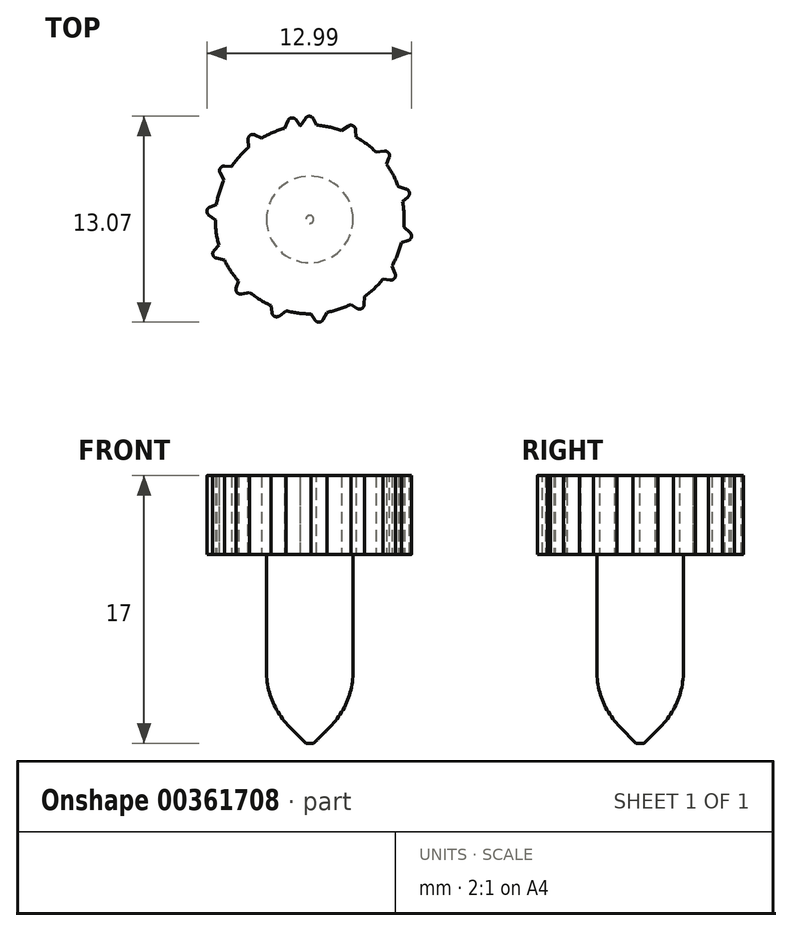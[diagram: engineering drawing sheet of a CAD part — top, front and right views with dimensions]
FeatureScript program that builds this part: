
annotation { "Feature Type Name" : "Feature", "Feature Type Description" : "" }
export const myFeature = defineFeature(function(context is Context, id is Id, definition is map)
    precondition{}
    {
        {
            var Q0;
            Q0=qCreatedBy(makeId("Top.planeOp"),FACE);
            var sketch = newSketch(context, id + "F0", { "sketchPlane" : qUnion([Q0])});
            skCircle(sketch, "E0", {"center": v(0, 0) * mm, "radius": 2.75 * mm});
            skSolve(sketch);
        }
        {
            var Q0;
            Q0 = qSketchRegion(id + "F0", true);
            extrude(context, id + "F1", {"entities" : qUnion([Q0]), "depth" : 12 * mm});
        }
        {
            var Q0;
            Q0=makeQuery(id+"F1.opExtrude","CAP_FACE",FACE,{"disambiguationData":[OSD([sQuery(id+"F0.wireOp",EDGE,"E0")])],"isStart":false});
            var sketch = newSketch(context, id + "F2", { "sketchPlane" : qUnion([Q0])});
            skCircle(sketch, "E1", {"center": v(0, 0) * mm, "radius": 6 * mm});
            skSolve(sketch);
        }
        {
            var Q0;
            Q0=makeQuery(id+"F2.imprint","IMPRINT",FACE,{"disambiguationData":[TD([[makeQuery(id+"F2.imprint","IMPRINT",EDGE,{"derivedFrom":sQuery(id+"F2.wireOp",EDGE,"E1")}),1.0]])]});
            var Q1;
            Q1=makeQuery(id+"F2.imprint","IMPRINT",FACE,{"disambiguationData":[TD([[makeQuery(id+"F2.imprint","IMPRINT",EDGE,{"derivedFrom":makeQuery(id+"F1.opExtrude","CAP_EDGE",EDGE,{"disambiguationData":[OSD([sQuery(id+"F0.wireOp",EDGE,"E0")])],"isStart":false})}),1.0]])]});
            extrude(context, id + "F3", {"entities" : qUnion([Q0, Q1]), "operationType" : NewBodyOperationType.ADD, "depth" : 5 * mm});
        }
        {
            var Q0;
            Q0=makeQuery(id+"F3.opExtrude","CAP_FACE",FACE,{"disambiguationData":[OSD([sQuery(id+"F2.wireOp",EDGE,"E1")])],"isStart":false});
            var sketch = newSketch(context, id + "F4", { "sketchPlane" : qUnion([Q0])});
            skLineSegment(sketch, "E2", {"start": v(-0.66, 5.85) * mm, "end": v(0, 6.85) * mm});
            skLineSegment(sketch, "E3", {"start": v(0, 6.85) * mm, "end": v(0.54, 5.78) * mm});
            skLineSegment(sketch, "E4", {"start": v(0.54, 5.78) * mm, "end": v(-0.66, 5.85) * mm});
            skLineSegment(sketch, "E5", {"start": v(-0.53, 6.04) * mm, "end": v(0.44, 5.98) * mm});
            skLineSegment(sketch, "E6.1.0", {"start": v(1.87, 5.58) * mm, "end": v(2.9, 6.2) * mm});
            skLineSegment(sketch, "E6.1.1", {"start": v(2.9, 6.2) * mm, "end": v(2.93, 5) * mm});
            skLineSegment(sketch, "E6.1.2", {"start": v(2.93, 5) * mm, "end": v(1.87, 5.58) * mm});
            skLineSegment(sketch, "E6.1.3", {"start": v(2.07, 5.7) * mm, "end": v(2.92, 5.24) * mm});
            skLineSegment(sketch, "E6.2.0", {"start": v(4.06, 4.26) * mm, "end": v(5.25, 4.4) * mm});
            skLineSegment(sketch, "E6.2.1", {"start": v(5.25, 4.4) * mm, "end": v(4.77, 3.3) * mm});
            skLineSegment(sketch, "E6.2.2", {"start": v(4.77, 3.3) * mm, "end": v(4.06, 4.26) * mm});
            skLineSegment(sketch, "E6.2.3", {"start": v(4.29, 4.3) * mm, "end": v(4.86, 3.51) * mm});
            skPoint(sketch, "E6.center", {"position": v(0, 0) * mm});
            skLineSegment(sketch, "E6.anchor1", {"start": v(0, 0) * mm, "end": v(-0.66, 5.85) * mm, "construction": true});
            skLineSegment(sketch, "E6.anchor2", {"start": v(0, 0) * mm, "end": v(-1.66, 5.64) * mm, "construction": true});
            skLineSegment(sketch, "E7.1.3.0", {"start": v(5.48, 2.15) * mm, "end": v(6.62, 1.77) * mm});
            skLineSegment(sketch, "E7.3.3.0", {"start": v(6.62, 1.77) * mm, "end": v(5.72, 0.97) * mm});
            skLineSegment(sketch, "E7.6.3.0", {"start": v(5.72, 0.97) * mm, "end": v(5.48, 2.15) * mm});
            skLineSegment(sketch, "E7.9.3.0", {"start": v(5.7, 2.08) * mm, "end": v(5.9, 1.13) * mm});
            skLineSegment(sketch, "E7.1.4.0", {"start": v(5.87, -0.37) * mm, "end": v(6.75, -1.19) * mm});
            skLineSegment(sketch, "E7.3.4.0", {"start": v(6.75, -1.19) * mm, "end": v(5.6, -1.53) * mm});
            skLineSegment(sketch, "E7.6.4.0", {"start": v(5.6, -1.53) * mm, "end": v(5.87, -0.37) * mm});
            skLineSegment(sketch, "E7.9.4.0", {"start": v(6.04, -0.52) * mm, "end": v(5.82, -1.47) * mm});
            skLineSegment(sketch, "E7.1.5.0", {"start": v(5.17, -2.81) * mm, "end": v(5.61, -3.93) * mm});
            skLineSegment(sketch, "E7.3.5.0", {"start": v(5.61, -3.93) * mm, "end": v(4.42, -3.76) * mm});
            skLineSegment(sketch, "E7.6.5.0", {"start": v(4.42, -3.76) * mm, "end": v(5.17, -2.81) * mm});
            skLineSegment(sketch, "E7.9.5.0", {"start": v(5.25, -3.03) * mm, "end": v(4.65, -3.79) * mm});
            skLineSegment(sketch, "E7.1.6.0", {"start": v(3.5, -4.73) * mm, "end": v(3.43, -5.93) * mm});
            skLineSegment(sketch, "E7.3.6.0", {"start": v(3.43, -5.93) * mm, "end": v(2.42, -5.27) * mm});
            skLineSegment(sketch, "E7.6.6.0", {"start": v(2.42, -5.27) * mm, "end": v(3.5, -4.73) * mm});
            skLineSegment(sketch, "E7.9.6.0", {"start": v(3.48, -4.97) * mm, "end": v(2.62, -5.4) * mm});
            skLineSegment(sketch, "E7.1.7.0", {"start": v(1.17, -5.77) * mm, "end": v(0.6, -6.82) * mm});
            skLineSegment(sketch, "E7.3.7.0", {"start": v(0.6, -6.82) * mm, "end": v(-0.03, -5.8) * mm});
            skLineSegment(sketch, "E7.6.7.0", {"start": v(-0.03, -5.8) * mm, "end": v(1.17, -5.77) * mm});
            skLineSegment(sketch, "E7.9.7.0", {"start": v(1.06, -5.97) * mm, "end": v(0.09, -6) * mm});
            skLineSegment(sketch, "E7.1.8.0", {"start": v(-1.38, -5.72) * mm, "end": v(-2.34, -6.44) * mm});
            skLineSegment(sketch, "E7.3.8.0", {"start": v(-2.34, -6.44) * mm, "end": v(-2.48, -5.25) * mm});
            skLineSegment(sketch, "E7.6.8.0", {"start": v(-2.48, -5.25) * mm, "end": v(-1.38, -5.72) * mm});
            skLineSegment(sketch, "E7.9.8.0", {"start": v(-1.57, -5.86) * mm, "end": v(-2.46, -5.48) * mm});
            skLineSegment(sketch, "E7.1.9.0", {"start": v(-3.67, -4.6) * mm, "end": v(-4.84, -4.84) * mm});
            skLineSegment(sketch, "E7.3.9.0", {"start": v(-4.84, -4.84) * mm, "end": v(-4.47, -3.7) * mm});
            skLineSegment(sketch, "E7.6.9.0", {"start": v(-4.47, -3.7) * mm, "end": v(-3.67, -4.6) * mm});
            skLineSegment(sketch, "E7.9.9.0", {"start": v(-3.9, -4.65) * mm, "end": v(-4.54, -3.92) * mm});
            skLineSegment(sketch, "E7.1.10.0", {"start": v(-5.27, -2.62) * mm, "end": v(-6.44, -2.34) * mm});
            skLineSegment(sketch, "E7.3.10.0", {"start": v(-6.44, -2.34) * mm, "end": v(-5.61, -1.47) * mm});
            skLineSegment(sketch, "E7.6.10.0", {"start": v(-5.61, -1.47) * mm, "end": v(-5.27, -2.62) * mm});
            skLineSegment(sketch, "E7.9.10.0", {"start": v(-5.5, -2.57) * mm, "end": v(-5.77, -1.64) * mm});
            skLineSegment(sketch, "E7.1.11.0", {"start": v(-5.88, -0.15) * mm, "end": v(-6.82, 0.6) * mm});
            skLineSegment(sketch, "E7.3.11.0", {"start": v(-6.82, 0.6) * mm, "end": v(-5.7, 1.04) * mm});
            skLineSegment(sketch, "E7.6.11.0", {"start": v(-5.7, 1.04) * mm, "end": v(-5.88, -0.15) * mm});
            skLineSegment(sketch, "E7.9.11.0", {"start": v(-6.06, 0) * mm, "end": v(-5.92, 0.96) * mm});
            skLineSegment(sketch, "E7.1.12.0", {"start": v(-5.4, 2.35) * mm, "end": v(-5.93, 3.43) * mm});
            skLineSegment(sketch, "E7.3.12.0", {"start": v(-5.93, 3.43) * mm, "end": v(-4.73, 3.36) * mm});
            skLineSegment(sketch, "E7.6.12.0", {"start": v(-4.73, 3.36) * mm, "end": v(-5.4, 2.35) * mm});
            skLineSegment(sketch, "E7.9.12.0", {"start": v(-5.5, 2.56) * mm, "end": v(-4.97, 3.37) * mm});
            skLineSegment(sketch, "E7.1.13.0", {"start": v(-3.9, 4.41) * mm, "end": v(-3.93, 5.61) * mm});
            skLineSegment(sketch, "E7.3.13.0", {"start": v(-3.93, 5.61) * mm, "end": v(-2.87, 5.04) * mm});
            skLineSegment(sketch, "E7.6.13.0", {"start": v(-2.87, 5.04) * mm, "end": v(-3.9, 4.41) * mm});
            skLineSegment(sketch, "E7.9.13.0", {"start": v(-3.9, 4.64) * mm, "end": v(-3.08, 5.15) * mm});
            skLineSegment(sketch, "E7.1.14.0", {"start": v(-1.66, 5.64) * mm, "end": v(-1.19, 6.75) * mm});
            skLineSegment(sketch, "E7.3.14.0", {"start": v(-1.19, 6.75) * mm, "end": v(-0.47, 5.78) * mm});
            skLineSegment(sketch, "E7.6.14.0", {"start": v(-0.47, 5.78) * mm, "end": v(-1.66, 5.64) * mm});
            skLineSegment(sketch, "E7.9.14.0", {"start": v(-1.57, 5.86) * mm, "end": v(-0.61, 5.97) * mm});
            skSolve(sketch);
        }
        {
            var Q0;
            {var subQ0=sQuery(id+"F4.wireOp",EDGE,"E3");var subQ1=sQuery(id+"F4.wireOp",EDGE,"E2");var subQ2=makeQuery(id+"F4.imprint","INTERSECT",VERTEX,{"derivedFrom":[subQ1,subQ0]});Q0=makeQuery(id+"F4.imprint","IMPRINT",FACE,{"disambiguationData":[TD([[makeQuery(id+"F4.imprint","IMPRINT",EDGE,{"disambiguationData":[TD([[subQ2,1.0]])],"derivedFrom":subQ1}),-1.0]])]});}
            var Q1;
            {var subQ0=sQuery(id+"F4.wireOp",EDGE,"E4");Q1=makeQuery(id+"F4.imprint","IMPRINT",FACE,{"disambiguationData":[TD([[makeQuery(id+"F4.imprint","IMPRINT",EDGE,{"derivedFrom":subQ0}),-1.0]])]});}
            var Q2;
            {var subQ0=sQuery(id+"F4.wireOp",EDGE,"E5");var subQ1=sQuery(id+"F4.wireOp",EDGE,"E3");var subQ2=makeQuery(id+"F4.imprint","INTERSECT",VERTEX,{"derivedFrom":[subQ1,subQ0]});Q2=makeQuery(id+"F4.imprint","IMPRINT",FACE,{"disambiguationData":[TD([[makeQuery(id+"F4.imprint","IMPRINT",EDGE,{"disambiguationData":[TD([[subQ2,-1.0]])],"derivedFrom":subQ1}),-1.0]])]});}
            var Q3;
            {var subQ0=sQuery(id+"F4.wireOp",EDGE,"E5");var subQ1=sQuery(id+"F4.wireOp",EDGE,"E2");var subQ2=makeQuery(id+"F4.imprint","INTERSECT",VERTEX,{"derivedFrom":[subQ1,subQ0]});Q3=makeQuery(id+"F4.imprint","IMPRINT",FACE,{"disambiguationData":[TD([[makeQuery(id+"F4.imprint","IMPRINT",EDGE,{"disambiguationData":[TD([[subQ2,1.0]])],"derivedFrom":subQ1}),-1.0]])]});}
            var Q4;
            {var subQ0=sQuery(id+"F4.wireOp",EDGE,"f33b821f-3d74-4163-88d8-381343337da1.3.27.0");var subQ1=sQuery(id+"F4.wireOp",EDGE,"f33b821f-3d74-4163-88d8-381343337da1.1.27.0");var subQ2=makeQuery(id+"F4.imprint","INTERSECT",VERTEX,{"derivedFrom":[subQ1,subQ0]});Q4=makeQuery(id+"F4.imprint","IMPRINT",FACE,{"disambiguationData":[TD([[makeQuery(id+"F4.imprint","IMPRINT",EDGE,{"disambiguationData":[TD([[subQ2,1.0]])],"derivedFrom":subQ1}),-1.0]])]});}
            var Q5;
            {var subQ0=sQuery(id+"F4.wireOp",EDGE,"f33b821f-3d74-4163-88d8-381343337da1.3.29.0");var subQ1=sQuery(id+"F4.wireOp",EDGE,"f33b821f-3d74-4163-88d8-381343337da1.1.29.0");var subQ2=makeQuery(id+"F4.imprint","INTERSECT",VERTEX,{"derivedFrom":[subQ1,subQ0]});Q5=makeQuery(id+"F4.imprint","IMPRINT",FACE,{"disambiguationData":[TD([[makeQuery(id+"F4.imprint","IMPRINT",EDGE,{"disambiguationData":[TD([[subQ2,1.0]])],"derivedFrom":subQ1}),-1.0]])]});}
            var Q6;
            {var subQ0=sQuery(id+"F4.wireOp",EDGE,"f33b821f-3d74-4163-88d8-381343337da1.3.26.0");var subQ1=sQuery(id+"F4.wireOp",EDGE,"f33b821f-3d74-4163-88d8-381343337da1.1.26.0");var subQ2=makeQuery(id+"F4.imprint","INTERSECT",VERTEX,{"derivedFrom":[subQ1,subQ0]});Q6=makeQuery(id+"F4.imprint","IMPRINT",FACE,{"disambiguationData":[TD([[makeQuery(id+"F4.imprint","IMPRINT",EDGE,{"disambiguationData":[TD([[subQ2,1.0]])],"derivedFrom":subQ1}),-1.0]])]});}
            var Q7;
            {var subQ0=sQuery(id+"F4.wireOp",EDGE,"E7.3.16.0");var subQ1=sQuery(id+"F4.wireOp",EDGE,"E7.1.16.0");var subQ2=makeQuery(id+"F4.imprint","INTERSECT",VERTEX,{"derivedFrom":[subQ1,subQ0]});Q7=makeQuery(id+"F4.imprint","IMPRINT",FACE,{"disambiguationData":[TD([[makeQuery(id+"F4.imprint","IMPRINT",EDGE,{"disambiguationData":[TD([[subQ2,1.0]])],"derivedFrom":subQ1}),-1.0]])]});}
            var Q8;
            {var subQ0=sQuery(id+"F4.wireOp",EDGE,"f33b821f-3d74-4163-88d8-381343337da1.3.21.0");var subQ1=sQuery(id+"F4.wireOp",EDGE,"f33b821f-3d74-4163-88d8-381343337da1.1.21.0");var subQ2=makeQuery(id+"F4.imprint","INTERSECT",VERTEX,{"derivedFrom":[subQ1,subQ0]});Q8=makeQuery(id+"F4.imprint","IMPRINT",FACE,{"disambiguationData":[TD([[makeQuery(id+"F4.imprint","IMPRINT",EDGE,{"disambiguationData":[TD([[subQ2,1.0]])],"derivedFrom":subQ1}),-1.0]])]});}
            var Q9;
            {var subQ0=sQuery(id+"F4.wireOp",EDGE,"f33b821f-3d74-4163-88d8-381343337da1.3.28.0");var subQ1=sQuery(id+"F4.wireOp",EDGE,"f33b821f-3d74-4163-88d8-381343337da1.1.28.0");var subQ2=makeQuery(id+"F4.imprint","INTERSECT",VERTEX,{"derivedFrom":[subQ1,subQ0]});Q9=makeQuery(id+"F4.imprint","IMPRINT",FACE,{"disambiguationData":[TD([[makeQuery(id+"F4.imprint","IMPRINT",EDGE,{"disambiguationData":[TD([[subQ2,1.0]])],"derivedFrom":subQ1}),-1.0]])]});}
            var Q10;
            {var subQ0=sQuery(id+"F4.wireOp",EDGE,"f33b821f-3d74-4163-88d8-381343337da1.3.25.0");var subQ1=sQuery(id+"F4.wireOp",EDGE,"f33b821f-3d74-4163-88d8-381343337da1.1.25.0");var subQ2=makeQuery(id+"F4.imprint","INTERSECT",VERTEX,{"derivedFrom":[subQ1,subQ0]});Q10=makeQuery(id+"F4.imprint","IMPRINT",FACE,{"disambiguationData":[TD([[makeQuery(id+"F4.imprint","IMPRINT",EDGE,{"disambiguationData":[TD([[subQ2,1.0]])],"derivedFrom":subQ1}),-1.0]])]});}
            var Q11;
            {var subQ0=sQuery(id+"F4.wireOp",EDGE,"f33b821f-3d74-4163-88d8-381343337da1.3.22.0");var subQ1=sQuery(id+"F4.wireOp",EDGE,"f33b821f-3d74-4163-88d8-381343337da1.1.22.0");var subQ2=makeQuery(id+"F4.imprint","INTERSECT",VERTEX,{"derivedFrom":[subQ1,subQ0]});Q11=makeQuery(id+"F4.imprint","IMPRINT",FACE,{"disambiguationData":[TD([[makeQuery(id+"F4.imprint","IMPRINT",EDGE,{"disambiguationData":[TD([[subQ2,1.0]])],"derivedFrom":subQ1}),-1.0]])]});}
            var Q12;
            {var subQ0=sQuery(id+"F4.wireOp",EDGE,"f33b821f-3d74-4163-88d8-381343337da1.3.23.0");var subQ1=sQuery(id+"F4.wireOp",EDGE,"f33b821f-3d74-4163-88d8-381343337da1.1.23.0");var subQ2=makeQuery(id+"F4.imprint","INTERSECT",VERTEX,{"derivedFrom":[subQ1,subQ0]});Q12=makeQuery(id+"F4.imprint","IMPRINT",FACE,{"disambiguationData":[TD([[makeQuery(id+"F4.imprint","IMPRINT",EDGE,{"disambiguationData":[TD([[subQ2,1.0]])],"derivedFrom":subQ1}),-1.0]])]});}
            var Q13;
            {var subQ0=sQuery(id+"F4.wireOp",EDGE,"f33b821f-3d74-4163-88d8-381343337da1.3.24.0");var subQ1=sQuery(id+"F4.wireOp",EDGE,"f33b821f-3d74-4163-88d8-381343337da1.1.24.0");var subQ2=makeQuery(id+"F4.imprint","INTERSECT",VERTEX,{"derivedFrom":[subQ1,subQ0]});Q13=makeQuery(id+"F4.imprint","IMPRINT",FACE,{"disambiguationData":[TD([[makeQuery(id+"F4.imprint","IMPRINT",EDGE,{"disambiguationData":[TD([[subQ2,1.0]])],"derivedFrom":subQ1}),-1.0]])]});}
            var Q14;
            {var subQ0=sQuery(id+"F4.wireOp",EDGE,"f33b821f-3d74-4163-88d8-381343337da1.3.20.0");var subQ1=sQuery(id+"F4.wireOp",EDGE,"f33b821f-3d74-4163-88d8-381343337da1.1.20.0");var subQ2=makeQuery(id+"F4.imprint","INTERSECT",VERTEX,{"derivedFrom":[subQ1,subQ0]});Q14=makeQuery(id+"F4.imprint","IMPRINT",FACE,{"disambiguationData":[TD([[makeQuery(id+"F4.imprint","IMPRINT",EDGE,{"disambiguationData":[TD([[subQ2,1.0]])],"derivedFrom":subQ1}),-1.0]])]});}
            var Q15;
            {var subQ0=sQuery(id+"F4.wireOp",EDGE,"E7.3.15.0");var subQ1=sQuery(id+"F4.wireOp",EDGE,"E7.1.15.0");var subQ2=makeQuery(id+"F4.imprint","INTERSECT",VERTEX,{"derivedFrom":[subQ1,subQ0]});Q15=makeQuery(id+"F4.imprint","IMPRINT",FACE,{"disambiguationData":[TD([[makeQuery(id+"F4.imprint","IMPRINT",EDGE,{"disambiguationData":[TD([[subQ2,1.0]])],"derivedFrom":subQ1}),-1.0]])]});}
            var Q16;
            {var subQ0=sQuery(id+"F4.wireOp",EDGE,"E7.3.19.0");var subQ1=sQuery(id+"F4.wireOp",EDGE,"E7.1.19.0");var subQ2=makeQuery(id+"F4.imprint","INTERSECT",VERTEX,{"derivedFrom":[subQ1,subQ0]});Q16=makeQuery(id+"F4.imprint","IMPRINT",FACE,{"disambiguationData":[TD([[makeQuery(id+"F4.imprint","IMPRINT",EDGE,{"disambiguationData":[TD([[subQ2,1.0]])],"derivedFrom":subQ1}),-1.0]])]});}
            var Q17;
            {var subQ0=sQuery(id+"F4.wireOp",EDGE,"E7.3.18.0");var subQ1=sQuery(id+"F4.wireOp",EDGE,"E7.1.18.0");var subQ2=makeQuery(id+"F4.imprint","INTERSECT",VERTEX,{"derivedFrom":[subQ1,subQ0]});Q17=makeQuery(id+"F4.imprint","IMPRINT",FACE,{"disambiguationData":[TD([[makeQuery(id+"F4.imprint","IMPRINT",EDGE,{"disambiguationData":[TD([[subQ2,1.0]])],"derivedFrom":subQ1}),-1.0]])]});}
            var Q18;
            {var subQ0=sQuery(id+"F4.wireOp",EDGE,"E7.3.17.0");var subQ1=sQuery(id+"F4.wireOp",EDGE,"E7.1.17.0");var subQ2=makeQuery(id+"F4.imprint","INTERSECT",VERTEX,{"derivedFrom":[subQ1,subQ0]});Q18=makeQuery(id+"F4.imprint","IMPRINT",FACE,{"disambiguationData":[TD([[makeQuery(id+"F4.imprint","IMPRINT",EDGE,{"disambiguationData":[TD([[subQ2,1.0]])],"derivedFrom":subQ1}),-1.0]])]});}
            var Q19;
            {var subQ0=sQuery(id+"F4.wireOp",EDGE,"E7.3.12.0");var subQ1=sQuery(id+"F4.wireOp",EDGE,"E7.1.12.0");var subQ2=makeQuery(id+"F4.imprint","INTERSECT",VERTEX,{"derivedFrom":[subQ1,subQ0]});Q19=makeQuery(id+"F4.imprint","IMPRINT",FACE,{"disambiguationData":[TD([[makeQuery(id+"F4.imprint","IMPRINT",EDGE,{"disambiguationData":[TD([[subQ2,1.0]])],"derivedFrom":subQ1}),-1.0]])]});}
            var Q20;
            {var subQ0=sQuery(id+"F4.wireOp",EDGE,"E7.3.11.0");var subQ1=sQuery(id+"F4.wireOp",EDGE,"E7.1.11.0");var subQ2=makeQuery(id+"F4.imprint","INTERSECT",VERTEX,{"derivedFrom":[subQ1,subQ0]});Q20=makeQuery(id+"F4.imprint","IMPRINT",FACE,{"disambiguationData":[TD([[makeQuery(id+"F4.imprint","IMPRINT",EDGE,{"disambiguationData":[TD([[subQ2,1.0]])],"derivedFrom":subQ1}),-1.0]])]});}
            var Q21;
            {var subQ0=sQuery(id+"F4.wireOp",EDGE,"E7.3.10.0");var subQ1=sQuery(id+"F4.wireOp",EDGE,"E7.1.10.0");var subQ2=makeQuery(id+"F4.imprint","INTERSECT",VERTEX,{"derivedFrom":[subQ1,subQ0]});Q21=makeQuery(id+"F4.imprint","IMPRINT",FACE,{"disambiguationData":[TD([[makeQuery(id+"F4.imprint","IMPRINT",EDGE,{"disambiguationData":[TD([[subQ2,1.0]])],"derivedFrom":subQ1}),-1.0]])]});}
            var Q22;
            {var subQ0=sQuery(id+"F4.wireOp",EDGE,"E7.3.8.0");var subQ1=sQuery(id+"F4.wireOp",EDGE,"E7.1.8.0");var subQ2=makeQuery(id+"F4.imprint","INTERSECT",VERTEX,{"derivedFrom":[subQ1,subQ0]});Q22=makeQuery(id+"F4.imprint","IMPRINT",FACE,{"disambiguationData":[TD([[makeQuery(id+"F4.imprint","IMPRINT",EDGE,{"disambiguationData":[TD([[subQ2,1.0]])],"derivedFrom":subQ1}),-1.0]])]});}
            var Q23;
            {var subQ0=sQuery(id+"F4.wireOp",EDGE,"E7.3.7.0");var subQ1=sQuery(id+"F4.wireOp",EDGE,"E7.1.7.0");var subQ2=makeQuery(id+"F4.imprint","INTERSECT",VERTEX,{"derivedFrom":[subQ1,subQ0]});Q23=makeQuery(id+"F4.imprint","IMPRINT",FACE,{"disambiguationData":[TD([[makeQuery(id+"F4.imprint","IMPRINT",EDGE,{"disambiguationData":[TD([[subQ2,1.0]])],"derivedFrom":subQ1}),-1.0]])]});}
            var Q24;
            {var subQ0=sQuery(id+"F4.wireOp",EDGE,"E7.3.6.0");var subQ1=sQuery(id+"F4.wireOp",EDGE,"E7.1.6.0");var subQ2=makeQuery(id+"F4.imprint","INTERSECT",VERTEX,{"derivedFrom":[subQ1,subQ0]});Q24=makeQuery(id+"F4.imprint","IMPRINT",FACE,{"disambiguationData":[TD([[makeQuery(id+"F4.imprint","IMPRINT",EDGE,{"disambiguationData":[TD([[subQ2,1.0]])],"derivedFrom":subQ1}),-1.0]])]});}
            var Q25;
            {var subQ0=sQuery(id+"F4.wireOp",EDGE,"E7.3.5.0");var subQ1=sQuery(id+"F4.wireOp",EDGE,"E7.1.5.0");var subQ2=makeQuery(id+"F4.imprint","INTERSECT",VERTEX,{"derivedFrom":[subQ1,subQ0]});Q25=makeQuery(id+"F4.imprint","IMPRINT",FACE,{"disambiguationData":[TD([[makeQuery(id+"F4.imprint","IMPRINT",EDGE,{"disambiguationData":[TD([[subQ2,1.0]])],"derivedFrom":subQ1}),-1.0]])]});}
            var Q26;
            {var subQ0=sQuery(id+"F4.wireOp",EDGE,"E7.3.4.0");var subQ1=sQuery(id+"F4.wireOp",EDGE,"E7.1.4.0");var subQ2=makeQuery(id+"F4.imprint","INTERSECT",VERTEX,{"derivedFrom":[subQ1,subQ0]});Q26=makeQuery(id+"F4.imprint","IMPRINT",FACE,{"disambiguationData":[TD([[makeQuery(id+"F4.imprint","IMPRINT",EDGE,{"disambiguationData":[TD([[subQ2,1.0]])],"derivedFrom":subQ1}),-1.0]])]});}
            var Q27;
            {var subQ0=sQuery(id+"F4.wireOp",EDGE,"E7.3.3.0");var subQ1=sQuery(id+"F4.wireOp",EDGE,"E7.1.3.0");var subQ2=makeQuery(id+"F4.imprint","INTERSECT",VERTEX,{"derivedFrom":[subQ1,subQ0]});Q27=makeQuery(id+"F4.imprint","IMPRINT",FACE,{"disambiguationData":[TD([[makeQuery(id+"F4.imprint","IMPRINT",EDGE,{"disambiguationData":[TD([[subQ2,1.0]])],"derivedFrom":subQ1}),-1.0]])]});}
            var Q28;
            {var subQ0=sQuery(id+"F4.wireOp",EDGE,"E6.2.1");var subQ1=sQuery(id+"F4.wireOp",EDGE,"E6.2.0");var subQ2=makeQuery(id+"F4.imprint","INTERSECT",VERTEX,{"derivedFrom":[subQ1,subQ0]});Q28=makeQuery(id+"F4.imprint","IMPRINT",FACE,{"disambiguationData":[TD([[makeQuery(id+"F4.imprint","IMPRINT",EDGE,{"disambiguationData":[TD([[subQ2,1.0]])],"derivedFrom":subQ1}),-1.0]])]});}
            var Q29;
            {var subQ0=sQuery(id+"F4.wireOp",EDGE,"E6.1.1");var subQ1=sQuery(id+"F4.wireOp",EDGE,"E6.1.0");var subQ2=makeQuery(id+"F4.imprint","INTERSECT",VERTEX,{"derivedFrom":[subQ1,subQ0]});Q29=makeQuery(id+"F4.imprint","IMPRINT",FACE,{"disambiguationData":[TD([[makeQuery(id+"F4.imprint","IMPRINT",EDGE,{"disambiguationData":[TD([[subQ2,1.0]])],"derivedFrom":subQ1}),-1.0]])]});}
            var Q30;
            {var subQ0=sQuery(id+"F4.wireOp",EDGE,"E7.3.14.0");var subQ1=sQuery(id+"F4.wireOp",EDGE,"E7.1.14.0");var subQ2=makeQuery(id+"F4.imprint","INTERSECT",VERTEX,{"derivedFrom":[subQ1,subQ0]});Q30=makeQuery(id+"F4.imprint","IMPRINT",FACE,{"disambiguationData":[TD([[makeQuery(id+"F4.imprint","IMPRINT",EDGE,{"disambiguationData":[TD([[subQ2,1.0]])],"derivedFrom":subQ1}),-1.0]])]});}
            var Q31;
            {var subQ0=sQuery(id+"F4.wireOp",EDGE,"E7.3.13.0");var subQ1=sQuery(id+"F4.wireOp",EDGE,"E7.1.13.0");var subQ2=makeQuery(id+"F4.imprint","INTERSECT",VERTEX,{"derivedFrom":[subQ1,subQ0]});Q31=makeQuery(id+"F4.imprint","IMPRINT",FACE,{"disambiguationData":[TD([[makeQuery(id+"F4.imprint","IMPRINT",EDGE,{"disambiguationData":[TD([[subQ2,1.0]])],"derivedFrom":subQ1}),-1.0]])]});}
            var Q32;
            {var subQ0=sQuery(id+"F4.wireOp",EDGE,"E7.9.6.0");var subQ1=sQuery(id+"F4.wireOp",EDGE,"E7.3.6.0");var subQ2=makeQuery(id+"F4.imprint","INTERSECT",VERTEX,{"derivedFrom":[subQ1,subQ0]});Q32=makeQuery(id+"F4.imprint","IMPRINT",FACE,{"disambiguationData":[TD([[makeQuery(id+"F4.imprint","IMPRINT",EDGE,{"disambiguationData":[TD([[subQ2,-1.0]])],"derivedFrom":subQ1}),-1.0]])]});}
            var Q33;
            {var subQ4=sQuery(id+"F4.wireOp",EDGE,"E7.6.4.0");Q33=makeQuery(id+"F4.imprint","IMPRINT",FACE,{"disambiguationData":[TD([[makeQuery(id+"F4.imprint","IMPRINT",EDGE,{"derivedFrom":subQ4}),-1.0]])]});}
            var Q34;
            {var subQ4=sQuery(id+"F4.wireOp",EDGE,"E7.6.17.0");Q34=makeQuery(id+"F4.imprint","IMPRINT",FACE,{"disambiguationData":[TD([[makeQuery(id+"F4.imprint","IMPRINT",EDGE,{"derivedFrom":subQ4}),-1.0]])]});}
            var Q35;
            {var subQ4=sQuery(id+"F4.wireOp",EDGE,"E6.1.2");Q35=makeQuery(id+"F4.imprint","IMPRINT",FACE,{"disambiguationData":[TD([[makeQuery(id+"F4.imprint","IMPRINT",EDGE,{"derivedFrom":subQ4}),-1.0]])]});}
            var Q36;
            {var subQ0=sQuery(id+"F4.wireOp",EDGE,"f33b821f-3d74-4163-88d8-381343337da1.9.22.0");var subQ1=sQuery(id+"F4.wireOp",EDGE,"f33b821f-3d74-4163-88d8-381343337da1.3.22.0");var subQ2=makeQuery(id+"F4.imprint","INTERSECT",VERTEX,{"derivedFrom":[subQ1,subQ0]});Q36=makeQuery(id+"F4.imprint","IMPRINT",FACE,{"disambiguationData":[TD([[makeQuery(id+"F4.imprint","IMPRINT",EDGE,{"disambiguationData":[TD([[subQ2,-1.0]])],"derivedFrom":subQ1}),-1.0]])]});}
            var Q37;
            {var subQ0=sQuery(id+"F4.wireOp",EDGE,"f33b821f-3d74-4163-88d8-381343337da1.6.20.0");Q37=makeQuery(id+"F4.imprint","IMPRINT",FACE,{"disambiguationData":[TD([[makeQuery(id+"F4.imprint","IMPRINT",EDGE,{"derivedFrom":subQ0}),-1.0]])]});}
            var Q38;
            {var subQ4=sQuery(id+"F4.wireOp",EDGE,"E7.6.3.0");Q38=makeQuery(id+"F4.imprint","IMPRINT",FACE,{"disambiguationData":[TD([[makeQuery(id+"F4.imprint","IMPRINT",EDGE,{"derivedFrom":subQ4}),-1.0]])]});}
            var Q39;
            {var subQ4=sQuery(id+"F4.wireOp",EDGE,"E7.6.19.0");Q39=makeQuery(id+"F4.imprint","IMPRINT",FACE,{"disambiguationData":[TD([[makeQuery(id+"F4.imprint","IMPRINT",EDGE,{"derivedFrom":subQ4}),-1.0]])]});}
            var Q40;
            {var subQ0=sQuery(id+"F4.wireOp",EDGE,"E7.6.15.0");Q40=makeQuery(id+"F4.imprint","IMPRINT",FACE,{"disambiguationData":[TD([[makeQuery(id+"F4.imprint","IMPRINT",EDGE,{"derivedFrom":subQ0}),-1.0]])]});}
            var Q41;
            {var subQ0=sQuery(id+"F4.wireOp",EDGE,"f33b821f-3d74-4163-88d8-381343337da1.9.22.0");var subQ1=sQuery(id+"F4.wireOp",EDGE,"f33b821f-3d74-4163-88d8-381343337da1.1.22.0");var subQ2=makeQuery(id+"F4.imprint","INTERSECT",VERTEX,{"derivedFrom":[subQ1,subQ0]});Q41=makeQuery(id+"F4.imprint","IMPRINT",FACE,{"disambiguationData":[TD([[makeQuery(id+"F4.imprint","IMPRINT",EDGE,{"disambiguationData":[TD([[subQ2,1.0]])],"derivedFrom":subQ1}),-1.0]])]});}
            var Q42;
            {var subQ4=sQuery(id+"F4.wireOp",EDGE,"E7.6.16.0");Q42=makeQuery(id+"F4.imprint","IMPRINT",FACE,{"disambiguationData":[TD([[makeQuery(id+"F4.imprint","IMPRINT",EDGE,{"derivedFrom":subQ4}),-1.0]])]});}
            var Q43;
            {var subQ0=sQuery(id+"F4.wireOp",EDGE,"E7.9.16.0");var subQ1=sQuery(id+"F4.wireOp",EDGE,"E7.3.16.0");var subQ2=makeQuery(id+"F4.imprint","INTERSECT",VERTEX,{"derivedFrom":[subQ1,subQ0]});Q43=makeQuery(id+"F4.imprint","IMPRINT",FACE,{"disambiguationData":[TD([[makeQuery(id+"F4.imprint","IMPRINT",EDGE,{"disambiguationData":[TD([[subQ2,-1.0]])],"derivedFrom":subQ1}),-1.0]])]});}
            var Q44;
            {var subQ4=sQuery(id+"F4.wireOp",EDGE,"f33b821f-3d74-4163-88d8-381343337da1.6.22.0");Q44=makeQuery(id+"F4.imprint","IMPRINT",FACE,{"disambiguationData":[TD([[makeQuery(id+"F4.imprint","IMPRINT",EDGE,{"derivedFrom":subQ4}),-1.0]])]});}
            var Q45;
            {var subQ0=sQuery(id+"F4.wireOp",EDGE,"E7.9.17.0");var subQ1=sQuery(id+"F4.wireOp",EDGE,"E7.1.17.0");var subQ2=makeQuery(id+"F4.imprint","INTERSECT",VERTEX,{"derivedFrom":[subQ1,subQ0]});Q45=makeQuery(id+"F4.imprint","IMPRINT",FACE,{"disambiguationData":[TD([[makeQuery(id+"F4.imprint","IMPRINT",EDGE,{"disambiguationData":[TD([[subQ2,1.0]])],"derivedFrom":subQ1}),-1.0]])]});}
            var Q46;
            {var subQ0=sQuery(id+"F4.wireOp",EDGE,"f33b821f-3d74-4163-88d8-381343337da1.9.25.0");var subQ1=sQuery(id+"F4.wireOp",EDGE,"f33b821f-3d74-4163-88d8-381343337da1.1.25.0");var subQ2=makeQuery(id+"F4.imprint","INTERSECT",VERTEX,{"derivedFrom":[subQ1,subQ0]});Q46=makeQuery(id+"F4.imprint","IMPRINT",FACE,{"disambiguationData":[TD([[makeQuery(id+"F4.imprint","IMPRINT",EDGE,{"disambiguationData":[TD([[subQ2,1.0]])],"derivedFrom":subQ1}),-1.0]])]});}
            var Q47;
            {var subQ0=sQuery(id+"F4.wireOp",EDGE,"f33b821f-3d74-4163-88d8-381343337da1.9.21.0");var subQ1=sQuery(id+"F4.wireOp",EDGE,"f33b821f-3d74-4163-88d8-381343337da1.3.21.0");var subQ2=makeQuery(id+"F4.imprint","INTERSECT",VERTEX,{"derivedFrom":[subQ1,subQ0]});Q47=makeQuery(id+"F4.imprint","IMPRINT",FACE,{"disambiguationData":[TD([[makeQuery(id+"F4.imprint","IMPRINT",EDGE,{"disambiguationData":[TD([[subQ2,-1.0]])],"derivedFrom":subQ1}),-1.0]])]});}
            var Q48;
            {var subQ4=sQuery(id+"F4.wireOp",EDGE,"f33b821f-3d74-4163-88d8-381343337da1.6.21.0");Q48=makeQuery(id+"F4.imprint","IMPRINT",FACE,{"disambiguationData":[TD([[makeQuery(id+"F4.imprint","IMPRINT",EDGE,{"derivedFrom":subQ4}),-1.0]])]});}
            var Q49;
            {var subQ4=sQuery(id+"F4.wireOp",EDGE,"E7.6.11.0");Q49=makeQuery(id+"F4.imprint","IMPRINT",FACE,{"disambiguationData":[TD([[makeQuery(id+"F4.imprint","IMPRINT",EDGE,{"derivedFrom":subQ4}),-1.0]])]});}
            var Q50;
            {var subQ4=sQuery(id+"F4.wireOp",EDGE,"E6.2.2");Q50=makeQuery(id+"F4.imprint","IMPRINT",FACE,{"disambiguationData":[TD([[makeQuery(id+"F4.imprint","IMPRINT",EDGE,{"derivedFrom":subQ4}),-1.0]])]});}
            var Q51;
            {var subQ0=sQuery(id+"F4.wireOp",EDGE,"E7.9.4.0");var subQ1=sQuery(id+"F4.wireOp",EDGE,"E7.1.4.0");var subQ2=makeQuery(id+"F4.imprint","INTERSECT",VERTEX,{"derivedFrom":[subQ1,subQ0]});Q51=makeQuery(id+"F4.imprint","IMPRINT",FACE,{"disambiguationData":[TD([[makeQuery(id+"F4.imprint","IMPRINT",EDGE,{"disambiguationData":[TD([[subQ2,1.0]])],"derivedFrom":subQ1}),-1.0]])]});}
            var Q52;
            {var subQ4=sQuery(id+"F4.wireOp",EDGE,"f33b821f-3d74-4163-88d8-381343337da1.6.28.0");Q52=makeQuery(id+"F4.imprint","IMPRINT",FACE,{"disambiguationData":[TD([[makeQuery(id+"F4.imprint","IMPRINT",EDGE,{"derivedFrom":subQ4}),-1.0]])]});}
            var Q53;
            {var subQ4=sQuery(id+"F4.wireOp",EDGE,"E7.6.12.0");Q53=makeQuery(id+"F4.imprint","IMPRINT",FACE,{"disambiguationData":[TD([[makeQuery(id+"F4.imprint","IMPRINT",EDGE,{"derivedFrom":subQ4}),-1.0]])]});}
            var Q54;
            {var subQ0=sQuery(id+"F4.wireOp",EDGE,"f33b821f-3d74-4163-88d8-381343337da1.9.28.0");var subQ1=sQuery(id+"F4.wireOp",EDGE,"f33b821f-3d74-4163-88d8-381343337da1.1.28.0");var subQ2=makeQuery(id+"F4.imprint","INTERSECT",VERTEX,{"derivedFrom":[subQ1,subQ0]});Q54=makeQuery(id+"F4.imprint","IMPRINT",FACE,{"disambiguationData":[TD([[makeQuery(id+"F4.imprint","IMPRINT",EDGE,{"disambiguationData":[TD([[subQ2,1.0]])],"derivedFrom":subQ1}),-1.0]])]});}
            var Q55;
            {var subQ0=sQuery(id+"F4.wireOp",EDGE,"f33b821f-3d74-4163-88d8-381343337da1.9.20.0");var subQ1=sQuery(id+"F4.wireOp",EDGE,"f33b821f-3d74-4163-88d8-381343337da1.1.20.0");var subQ2=makeQuery(id+"F4.imprint","INTERSECT",VERTEX,{"derivedFrom":[subQ1,subQ0]});Q55=makeQuery(id+"F4.imprint","IMPRINT",FACE,{"disambiguationData":[TD([[makeQuery(id+"F4.imprint","IMPRINT",EDGE,{"disambiguationData":[TD([[subQ2,1.0]])],"derivedFrom":subQ1}),-1.0]])]});}
            var Q56;
            {var subQ0=sQuery(id+"F4.wireOp",EDGE,"E7.9.4.0");var subQ1=sQuery(id+"F4.wireOp",EDGE,"E7.3.4.0");var subQ2=makeQuery(id+"F4.imprint","INTERSECT",VERTEX,{"derivedFrom":[subQ1,subQ0]});Q56=makeQuery(id+"F4.imprint","IMPRINT",FACE,{"disambiguationData":[TD([[makeQuery(id+"F4.imprint","IMPRINT",EDGE,{"disambiguationData":[TD([[subQ2,-1.0]])],"derivedFrom":subQ1}),-1.0]])]});}
            var Q57;
            {var subQ4=sQuery(id+"F4.wireOp",EDGE,"f33b821f-3d74-4163-88d8-381343337da1.6.29.0");Q57=makeQuery(id+"F4.imprint","IMPRINT",FACE,{"disambiguationData":[TD([[makeQuery(id+"F4.imprint","IMPRINT",EDGE,{"derivedFrom":subQ4}),-1.0]])]});}
            var Q58;
            {var subQ4=sQuery(id+"F4.wireOp",EDGE,"E7.6.13.0");Q58=makeQuery(id+"F4.imprint","IMPRINT",FACE,{"disambiguationData":[TD([[makeQuery(id+"F4.imprint","IMPRINT",EDGE,{"derivedFrom":subQ4}),-1.0]])]});}
            var Q59;
            {var subQ0=sQuery(id+"F4.wireOp",EDGE,"f33b821f-3d74-4163-88d8-381343337da1.9.20.0");var subQ1=sQuery(id+"F4.wireOp",EDGE,"f33b821f-3d74-4163-88d8-381343337da1.3.20.0");var subQ2=makeQuery(id+"F4.imprint","INTERSECT",VERTEX,{"derivedFrom":[subQ1,subQ0]});Q59=makeQuery(id+"F4.imprint","IMPRINT",FACE,{"disambiguationData":[TD([[makeQuery(id+"F4.imprint","IMPRINT",EDGE,{"disambiguationData":[TD([[subQ2,-1.0]])],"derivedFrom":subQ1}),-1.0]])]});}
            var Q60;
            {var subQ4=sQuery(id+"F4.wireOp",EDGE,"E7.6.14.0");Q60=makeQuery(id+"F4.imprint","IMPRINT",FACE,{"disambiguationData":[TD([[makeQuery(id+"F4.imprint","IMPRINT",EDGE,{"derivedFrom":subQ4}),-1.0]])]});}
            var Q61;
            {var subQ0=sQuery(id+"F4.wireOp",EDGE,"f33b821f-3d74-4163-88d8-381343337da1.9.21.0");var subQ1=sQuery(id+"F4.wireOp",EDGE,"f33b821f-3d74-4163-88d8-381343337da1.1.21.0");var subQ2=makeQuery(id+"F4.imprint","INTERSECT",VERTEX,{"derivedFrom":[subQ1,subQ0]});Q61=makeQuery(id+"F4.imprint","IMPRINT",FACE,{"disambiguationData":[TD([[makeQuery(id+"F4.imprint","IMPRINT",EDGE,{"disambiguationData":[TD([[subQ2,1.0]])],"derivedFrom":subQ1}),-1.0]])]});}
            var Q62;
            {var subQ4=sQuery(id+"F4.wireOp",EDGE,"f33b821f-3d74-4163-88d8-381343337da1.6.26.0");Q62=makeQuery(id+"F4.imprint","IMPRINT",FACE,{"disambiguationData":[TD([[makeQuery(id+"F4.imprint","IMPRINT",EDGE,{"derivedFrom":subQ4}),-1.0]])]});}
            var Q63;
            {var subQ0=sQuery(id+"F4.wireOp",EDGE,"f33b821f-3d74-4163-88d8-381343337da1.6.25.0");Q63=makeQuery(id+"F4.imprint","IMPRINT",FACE,{"disambiguationData":[TD([[makeQuery(id+"F4.imprint","IMPRINT",EDGE,{"derivedFrom":subQ0}),-1.0]])]});}
            var Q64;
            {var subQ0=sQuery(id+"F4.wireOp",EDGE,"E6.2.3");var subQ1=sQuery(id+"F4.wireOp",EDGE,"E6.2.1");var subQ2=makeQuery(id+"F4.imprint","INTERSECT",VERTEX,{"derivedFrom":[subQ1,subQ0]});Q64=makeQuery(id+"F4.imprint","IMPRINT",FACE,{"disambiguationData":[TD([[makeQuery(id+"F4.imprint","IMPRINT",EDGE,{"disambiguationData":[TD([[subQ2,-1.0]])],"derivedFrom":subQ1}),-1.0]])]});}
            var Q65;
            {var subQ4=sQuery(id+"F4.wireOp",EDGE,"E7.6.8.0");Q65=makeQuery(id+"F4.imprint","IMPRINT",FACE,{"disambiguationData":[TD([[makeQuery(id+"F4.imprint","IMPRINT",EDGE,{"derivedFrom":subQ4}),-1.0]])]});}
            var Q66;
            {var subQ4=sQuery(id+"F4.wireOp",EDGE,"f33b821f-3d74-4163-88d8-381343337da1.6.24.0");Q66=makeQuery(id+"F4.imprint","IMPRINT",FACE,{"disambiguationData":[TD([[makeQuery(id+"F4.imprint","IMPRINT",EDGE,{"derivedFrom":subQ4}),-1.0]])]});}
            var Q67;
            {var subQ0=sQuery(id+"F4.wireOp",EDGE,"E6.2.3");var subQ1=sQuery(id+"F4.wireOp",EDGE,"E6.2.0");var subQ2=makeQuery(id+"F4.imprint","INTERSECT",VERTEX,{"derivedFrom":[subQ1,subQ0]});Q67=makeQuery(id+"F4.imprint","IMPRINT",FACE,{"disambiguationData":[TD([[makeQuery(id+"F4.imprint","IMPRINT",EDGE,{"disambiguationData":[TD([[subQ2,1.0]])],"derivedFrom":subQ1}),-1.0]])]});}
            var Q68;
            {var subQ4=sQuery(id+"F4.wireOp",EDGE,"E7.6.7.0");Q68=makeQuery(id+"F4.imprint","IMPRINT",FACE,{"disambiguationData":[TD([[makeQuery(id+"F4.imprint","IMPRINT",EDGE,{"derivedFrom":subQ4}),-1.0]])]});}
            var Q69;
            {var subQ4=sQuery(id+"F4.wireOp",EDGE,"f33b821f-3d74-4163-88d8-381343337da1.6.23.0");Q69=makeQuery(id+"F4.imprint","IMPRINT",FACE,{"disambiguationData":[TD([[makeQuery(id+"F4.imprint","IMPRINT",EDGE,{"derivedFrom":subQ4}),-1.0]])]});}
            var Q70;
            {var subQ0=sQuery(id+"F4.wireOp",EDGE,"E6.1.3");var subQ1=sQuery(id+"F4.wireOp",EDGE,"E6.1.1");var subQ2=makeQuery(id+"F4.imprint","INTERSECT",VERTEX,{"derivedFrom":[subQ1,subQ0]});Q70=makeQuery(id+"F4.imprint","IMPRINT",FACE,{"disambiguationData":[TD([[makeQuery(id+"F4.imprint","IMPRINT",EDGE,{"disambiguationData":[TD([[subQ2,-1.0]])],"derivedFrom":subQ1}),-1.0]])]});}
            var Q71;
            {var subQ0=sQuery(id+"F4.wireOp",EDGE,"E7.9.17.0");var subQ1=sQuery(id+"F4.wireOp",EDGE,"E7.3.17.0");var subQ2=makeQuery(id+"F4.imprint","INTERSECT",VERTEX,{"derivedFrom":[subQ1,subQ0]});Q71=makeQuery(id+"F4.imprint","IMPRINT",FACE,{"disambiguationData":[TD([[makeQuery(id+"F4.imprint","IMPRINT",EDGE,{"disambiguationData":[TD([[subQ2,-1.0]])],"derivedFrom":subQ1}),-1.0]])]});}
            var Q72;
            {var subQ0=sQuery(id+"F4.wireOp",EDGE,"f33b821f-3d74-4163-88d8-381343337da1.9.25.0");var subQ1=sQuery(id+"F4.wireOp",EDGE,"f33b821f-3d74-4163-88d8-381343337da1.3.25.0");var subQ2=makeQuery(id+"F4.imprint","INTERSECT",VERTEX,{"derivedFrom":[subQ1,subQ0]});Q72=makeQuery(id+"F4.imprint","IMPRINT",FACE,{"disambiguationData":[TD([[makeQuery(id+"F4.imprint","IMPRINT",EDGE,{"disambiguationData":[TD([[subQ2,-1.0]])],"derivedFrom":subQ1}),-1.0]])]});}
            var Q73;
            {var subQ0=sQuery(id+"F4.wireOp",EDGE,"E7.3.9.0");var subQ1=sQuery(id+"F4.wireOp",EDGE,"E7.1.9.0");var subQ2=makeQuery(id+"F4.imprint","INTERSECT",VERTEX,{"derivedFrom":[subQ1,subQ0]});Q73=makeQuery(id+"F4.imprint","IMPRINT",FACE,{"disambiguationData":[TD([[makeQuery(id+"F4.imprint","IMPRINT",EDGE,{"disambiguationData":[TD([[subQ2,1.0]])],"derivedFrom":subQ1}),-1.0]])]});}
            var Q74;
            {var subQ0=sQuery(id+"F4.wireOp",EDGE,"E7.9.14.0");var subQ1=sQuery(id+"F4.wireOp",EDGE,"E7.3.14.0");var subQ2=makeQuery(id+"F4.imprint","INTERSECT",VERTEX,{"derivedFrom":[subQ1,subQ0]});Q74=makeQuery(id+"F4.imprint","IMPRINT",FACE,{"disambiguationData":[TD([[makeQuery(id+"F4.imprint","IMPRINT",EDGE,{"disambiguationData":[TD([[subQ2,-1.0]])],"derivedFrom":subQ1}),-1.0]])]});}
            var Q75;
            {var subQ0=sQuery(id+"F4.wireOp",EDGE,"f33b821f-3d74-4163-88d8-381343337da1.9.24.0");var subQ1=sQuery(id+"F4.wireOp",EDGE,"f33b821f-3d74-4163-88d8-381343337da1.1.24.0");var subQ2=makeQuery(id+"F4.imprint","INTERSECT",VERTEX,{"derivedFrom":[subQ1,subQ0]});Q75=makeQuery(id+"F4.imprint","IMPRINT",FACE,{"disambiguationData":[TD([[makeQuery(id+"F4.imprint","IMPRINT",EDGE,{"disambiguationData":[TD([[subQ2,1.0]])],"derivedFrom":subQ1}),-1.0]])]});}
            var Q76;
            {var subQ0=sQuery(id+"F4.wireOp",EDGE,"E7.9.16.0");var subQ1=sQuery(id+"F4.wireOp",EDGE,"E7.1.16.0");var subQ2=makeQuery(id+"F4.imprint","INTERSECT",VERTEX,{"derivedFrom":[subQ1,subQ0]});Q76=makeQuery(id+"F4.imprint","IMPRINT",FACE,{"disambiguationData":[TD([[makeQuery(id+"F4.imprint","IMPRINT",EDGE,{"disambiguationData":[TD([[subQ2,1.0]])],"derivedFrom":subQ1}),-1.0]])]});}
            var Q77;
            {var subQ0=sQuery(id+"F4.wireOp",EDGE,"E7.9.8.0");var subQ1=sQuery(id+"F4.wireOp",EDGE,"E7.1.8.0");var subQ2=makeQuery(id+"F4.imprint","INTERSECT",VERTEX,{"derivedFrom":[subQ1,subQ0]});Q77=makeQuery(id+"F4.imprint","IMPRINT",FACE,{"disambiguationData":[TD([[makeQuery(id+"F4.imprint","IMPRINT",EDGE,{"disambiguationData":[TD([[subQ2,1.0]])],"derivedFrom":subQ1}),-1.0]])]});}
            var Q78;
            {var subQ0=sQuery(id+"F4.wireOp",EDGE,"E7.9.15.0");var subQ1=sQuery(id+"F4.wireOp",EDGE,"E7.1.15.0");var subQ2=makeQuery(id+"F4.imprint","INTERSECT",VERTEX,{"derivedFrom":[subQ1,subQ0]});Q78=makeQuery(id+"F4.imprint","IMPRINT",FACE,{"disambiguationData":[TD([[makeQuery(id+"F4.imprint","IMPRINT",EDGE,{"disambiguationData":[TD([[subQ2,1.0]])],"derivedFrom":subQ1}),-1.0]])]});}
            var Q79;
            {var subQ0=sQuery(id+"F4.wireOp",EDGE,"E7.6.5.0");Q79=makeQuery(id+"F4.imprint","IMPRINT",FACE,{"disambiguationData":[TD([[makeQuery(id+"F4.imprint","IMPRINT",EDGE,{"derivedFrom":subQ0}),-1.0]])]});}
            var Q80;
            {var subQ0=sQuery(id+"F4.wireOp",EDGE,"E7.9.7.0");var subQ1=sQuery(id+"F4.wireOp",EDGE,"E7.3.7.0");var subQ2=makeQuery(id+"F4.imprint","INTERSECT",VERTEX,{"derivedFrom":[subQ1,subQ0]});Q80=makeQuery(id+"F4.imprint","IMPRINT",FACE,{"disambiguationData":[TD([[makeQuery(id+"F4.imprint","IMPRINT",EDGE,{"disambiguationData":[TD([[subQ2,-1.0]])],"derivedFrom":subQ1}),-1.0]])]});}
            var Q81;
            {var subQ0=sQuery(id+"F4.wireOp",EDGE,"E7.9.15.0");var subQ1=sQuery(id+"F4.wireOp",EDGE,"E7.3.15.0");var subQ2=makeQuery(id+"F4.imprint","INTERSECT",VERTEX,{"derivedFrom":[subQ1,subQ0]});Q81=makeQuery(id+"F4.imprint","IMPRINT",FACE,{"disambiguationData":[TD([[makeQuery(id+"F4.imprint","IMPRINT",EDGE,{"disambiguationData":[TD([[subQ2,-1.0]])],"derivedFrom":subQ1}),-1.0]])]});}
            var Q82;
            {var subQ0=sQuery(id+"F4.wireOp",EDGE,"f33b821f-3d74-4163-88d8-381343337da1.9.23.0");var subQ1=sQuery(id+"F4.wireOp",EDGE,"f33b821f-3d74-4163-88d8-381343337da1.3.23.0");var subQ2=makeQuery(id+"F4.imprint","INTERSECT",VERTEX,{"derivedFrom":[subQ1,subQ0]});Q82=makeQuery(id+"F4.imprint","IMPRINT",FACE,{"disambiguationData":[TD([[makeQuery(id+"F4.imprint","IMPRINT",EDGE,{"disambiguationData":[TD([[subQ2,-1.0]])],"derivedFrom":subQ1}),-1.0]])]});}
            var Q83;
            {var subQ0=sQuery(id+"F4.wireOp",EDGE,"f33b821f-3d74-4163-88d8-381343337da1.9.24.0");var subQ1=sQuery(id+"F4.wireOp",EDGE,"f33b821f-3d74-4163-88d8-381343337da1.3.24.0");var subQ2=makeQuery(id+"F4.imprint","INTERSECT",VERTEX,{"derivedFrom":[subQ1,subQ0]});Q83=makeQuery(id+"F4.imprint","IMPRINT",FACE,{"disambiguationData":[TD([[makeQuery(id+"F4.imprint","IMPRINT",EDGE,{"disambiguationData":[TD([[subQ2,-1.0]])],"derivedFrom":subQ1}),-1.0]])]});}
            var Q84;
            {var subQ0=sQuery(id+"F4.wireOp",EDGE,"E7.9.6.0");var subQ1=sQuery(id+"F4.wireOp",EDGE,"E7.1.6.0");var subQ2=makeQuery(id+"F4.imprint","INTERSECT",VERTEX,{"derivedFrom":[subQ1,subQ0]});Q84=makeQuery(id+"F4.imprint","IMPRINT",FACE,{"disambiguationData":[TD([[makeQuery(id+"F4.imprint","IMPRINT",EDGE,{"disambiguationData":[TD([[subQ2,1.0]])],"derivedFrom":subQ1}),-1.0]])]});}
            var Q85;
            {var subQ0=sQuery(id+"F4.wireOp",EDGE,"f33b821f-3d74-4163-88d8-381343337da1.9.29.0");var subQ1=sQuery(id+"F4.wireOp",EDGE,"f33b821f-3d74-4163-88d8-381343337da1.3.29.0");var subQ2=makeQuery(id+"F4.imprint","INTERSECT",VERTEX,{"derivedFrom":[subQ1,subQ0]});Q85=makeQuery(id+"F4.imprint","IMPRINT",FACE,{"disambiguationData":[TD([[makeQuery(id+"F4.imprint","IMPRINT",EDGE,{"disambiguationData":[TD([[subQ2,-1.0]])],"derivedFrom":subQ1}),-1.0]])]});}
            var Q86;
            {var subQ0=sQuery(id+"F4.wireOp",EDGE,"E7.9.14.0");var subQ1=sQuery(id+"F4.wireOp",EDGE,"E7.1.14.0");var subQ2=makeQuery(id+"F4.imprint","INTERSECT",VERTEX,{"derivedFrom":[subQ1,subQ0]});Q86=makeQuery(id+"F4.imprint","IMPRINT",FACE,{"disambiguationData":[TD([[makeQuery(id+"F4.imprint","IMPRINT",EDGE,{"disambiguationData":[TD([[subQ2,1.0]])],"derivedFrom":subQ1}),-1.0]])]});}
            var Q87;
            {var subQ4=sQuery(id+"F4.wireOp",EDGE,"E7.6.6.0");Q87=makeQuery(id+"F4.imprint","IMPRINT",FACE,{"disambiguationData":[TD([[makeQuery(id+"F4.imprint","IMPRINT",EDGE,{"derivedFrom":subQ4}),-1.0]])]});}
            var Q88;
            {var subQ0=sQuery(id+"F4.wireOp",EDGE,"E6.1.3");var subQ1=sQuery(id+"F4.wireOp",EDGE,"E6.1.0");var subQ2=makeQuery(id+"F4.imprint","INTERSECT",VERTEX,{"derivedFrom":[subQ1,subQ0]});Q88=makeQuery(id+"F4.imprint","IMPRINT",FACE,{"disambiguationData":[TD([[makeQuery(id+"F4.imprint","IMPRINT",EDGE,{"disambiguationData":[TD([[subQ2,1.0]])],"derivedFrom":subQ1}),-1.0]])]});}
            var Q89;
            {var subQ0=sQuery(id+"F4.wireOp",EDGE,"E7.9.8.0");var subQ1=sQuery(id+"F4.wireOp",EDGE,"E7.3.8.0");var subQ2=makeQuery(id+"F4.imprint","INTERSECT",VERTEX,{"derivedFrom":[subQ1,subQ0]});Q89=makeQuery(id+"F4.imprint","IMPRINT",FACE,{"disambiguationData":[TD([[makeQuery(id+"F4.imprint","IMPRINT",EDGE,{"disambiguationData":[TD([[subQ2,-1.0]])],"derivedFrom":subQ1}),-1.0]])]});}
            var Q90;
            {var subQ0=sQuery(id+"F4.wireOp",EDGE,"f33b821f-3d74-4163-88d8-381343337da1.9.27.0");var subQ1=sQuery(id+"F4.wireOp",EDGE,"f33b821f-3d74-4163-88d8-381343337da1.3.27.0");var subQ2=makeQuery(id+"F4.imprint","INTERSECT",VERTEX,{"derivedFrom":[subQ1,subQ0]});Q90=makeQuery(id+"F4.imprint","IMPRINT",FACE,{"disambiguationData":[TD([[makeQuery(id+"F4.imprint","IMPRINT",EDGE,{"disambiguationData":[TD([[subQ2,-1.0]])],"derivedFrom":subQ1}),-1.0]])]});}
            var Q91;
            {var subQ0=sQuery(id+"F4.wireOp",EDGE,"E7.9.19.0");var subQ1=sQuery(id+"F4.wireOp",EDGE,"E7.3.19.0");var subQ2=makeQuery(id+"F4.imprint","INTERSECT",VERTEX,{"derivedFrom":[subQ1,subQ0]});Q91=makeQuery(id+"F4.imprint","IMPRINT",FACE,{"disambiguationData":[TD([[makeQuery(id+"F4.imprint","IMPRINT",EDGE,{"disambiguationData":[TD([[subQ2,-1.0]])],"derivedFrom":subQ1}),-1.0]])]});}
            var Q92;
            {var subQ0=sQuery(id+"F4.wireOp",EDGE,"E7.9.11.0");var subQ1=sQuery(id+"F4.wireOp",EDGE,"E7.3.11.0");var subQ2=makeQuery(id+"F4.imprint","INTERSECT",VERTEX,{"derivedFrom":[subQ1,subQ0]});Q92=makeQuery(id+"F4.imprint","IMPRINT",FACE,{"disambiguationData":[TD([[makeQuery(id+"F4.imprint","IMPRINT",EDGE,{"disambiguationData":[TD([[subQ2,-1.0]])],"derivedFrom":subQ1}),-1.0]])]});}
            var Q93;
            {var subQ0=sQuery(id+"F4.wireOp",EDGE,"E7.9.7.0");var subQ1=sQuery(id+"F4.wireOp",EDGE,"E7.1.7.0");var subQ2=makeQuery(id+"F4.imprint","INTERSECT",VERTEX,{"derivedFrom":[subQ1,subQ0]});Q93=makeQuery(id+"F4.imprint","IMPRINT",FACE,{"disambiguationData":[TD([[makeQuery(id+"F4.imprint","IMPRINT",EDGE,{"disambiguationData":[TD([[subQ2,1.0]])],"derivedFrom":subQ1}),-1.0]])]});}
            var Q94;
            {var subQ0=sQuery(id+"F4.wireOp",EDGE,"E7.9.3.0");var subQ1=sQuery(id+"F4.wireOp",EDGE,"E7.3.3.0");var subQ2=makeQuery(id+"F4.imprint","INTERSECT",VERTEX,{"derivedFrom":[subQ1,subQ0]});Q94=makeQuery(id+"F4.imprint","IMPRINT",FACE,{"disambiguationData":[TD([[makeQuery(id+"F4.imprint","IMPRINT",EDGE,{"disambiguationData":[TD([[subQ2,-1.0]])],"derivedFrom":subQ1}),-1.0]])]});}
            var Q95;
            {var subQ4=sQuery(id+"F4.wireOp",EDGE,"f33b821f-3d74-4163-88d8-381343337da1.6.27.0");Q95=makeQuery(id+"F4.imprint","IMPRINT",FACE,{"disambiguationData":[TD([[makeQuery(id+"F4.imprint","IMPRINT",EDGE,{"derivedFrom":subQ4}),-1.0]])]});}
            var Q96;
            {var subQ4=sQuery(id+"F4.wireOp",EDGE,"E7.6.18.0");Q96=makeQuery(id+"F4.imprint","IMPRINT",FACE,{"disambiguationData":[TD([[makeQuery(id+"F4.imprint","IMPRINT",EDGE,{"derivedFrom":subQ4}),-1.0]])]});}
            var Q97;
            {var subQ0=sQuery(id+"F4.wireOp",EDGE,"E7.9.13.0");var subQ1=sQuery(id+"F4.wireOp",EDGE,"E7.3.13.0");var subQ2=makeQuery(id+"F4.imprint","INTERSECT",VERTEX,{"derivedFrom":[subQ1,subQ0]});Q97=makeQuery(id+"F4.imprint","IMPRINT",FACE,{"disambiguationData":[TD([[makeQuery(id+"F4.imprint","IMPRINT",EDGE,{"disambiguationData":[TD([[subQ2,-1.0]])],"derivedFrom":subQ1}),-1.0]])]});}
            var Q98;
            {var subQ0=sQuery(id+"F4.wireOp",EDGE,"E7.9.5.0");var subQ1=sQuery(id+"F4.wireOp",EDGE,"E7.3.5.0");var subQ2=makeQuery(id+"F4.imprint","INTERSECT",VERTEX,{"derivedFrom":[subQ1,subQ0]});Q98=makeQuery(id+"F4.imprint","IMPRINT",FACE,{"disambiguationData":[TD([[makeQuery(id+"F4.imprint","IMPRINT",EDGE,{"disambiguationData":[TD([[subQ2,-1.0]])],"derivedFrom":subQ1}),-1.0]])]});}
            var Q99;
            {var subQ0=sQuery(id+"F4.wireOp",EDGE,"E7.9.12.0");var subQ1=sQuery(id+"F4.wireOp",EDGE,"E7.1.12.0");var subQ2=makeQuery(id+"F4.imprint","INTERSECT",VERTEX,{"derivedFrom":[subQ1,subQ0]});Q99=makeQuery(id+"F4.imprint","IMPRINT",FACE,{"disambiguationData":[TD([[makeQuery(id+"F4.imprint","IMPRINT",EDGE,{"disambiguationData":[TD([[subQ2,1.0]])],"derivedFrom":subQ1}),-1.0]])]});}
            var Q100;
            {var subQ0=sQuery(id+"F4.wireOp",EDGE,"E7.9.12.0");var subQ1=sQuery(id+"F4.wireOp",EDGE,"E7.3.12.0");var subQ2=makeQuery(id+"F4.imprint","INTERSECT",VERTEX,{"derivedFrom":[subQ1,subQ0]});Q100=makeQuery(id+"F4.imprint","IMPRINT",FACE,{"disambiguationData":[TD([[makeQuery(id+"F4.imprint","IMPRINT",EDGE,{"disambiguationData":[TD([[subQ2,-1.0]])],"derivedFrom":subQ1}),-1.0]])]});}
            var Q101;
            {var subQ0=sQuery(id+"F4.wireOp",EDGE,"f33b821f-3d74-4163-88d8-381343337da1.9.28.0");var subQ1=sQuery(id+"F4.wireOp",EDGE,"f33b821f-3d74-4163-88d8-381343337da1.3.28.0");var subQ2=makeQuery(id+"F4.imprint","INTERSECT",VERTEX,{"derivedFrom":[subQ1,subQ0]});Q101=makeQuery(id+"F4.imprint","IMPRINT",FACE,{"disambiguationData":[TD([[makeQuery(id+"F4.imprint","IMPRINT",EDGE,{"disambiguationData":[TD([[subQ2,-1.0]])],"derivedFrom":subQ1}),-1.0]])]});}
            var Q102;
            {var subQ0=sQuery(id+"F4.wireOp",EDGE,"E7.9.13.0");var subQ1=sQuery(id+"F4.wireOp",EDGE,"E7.1.13.0");var subQ2=makeQuery(id+"F4.imprint","INTERSECT",VERTEX,{"derivedFrom":[subQ1,subQ0]});Q102=makeQuery(id+"F4.imprint","IMPRINT",FACE,{"disambiguationData":[TD([[makeQuery(id+"F4.imprint","IMPRINT",EDGE,{"disambiguationData":[TD([[subQ2,1.0]])],"derivedFrom":subQ1}),-1.0]])]});}
            var Q103;
            {var subQ0=sQuery(id+"F4.wireOp",EDGE,"E7.9.5.0");var subQ1=sQuery(id+"F4.wireOp",EDGE,"E7.1.5.0");var subQ2=makeQuery(id+"F4.imprint","INTERSECT",VERTEX,{"derivedFrom":[subQ1,subQ0]});Q103=makeQuery(id+"F4.imprint","IMPRINT",FACE,{"disambiguationData":[TD([[makeQuery(id+"F4.imprint","IMPRINT",EDGE,{"disambiguationData":[TD([[subQ2,1.0]])],"derivedFrom":subQ1}),-1.0]])]});}
            var Q104;
            {var subQ0=sQuery(id+"F4.wireOp",EDGE,"f33b821f-3d74-4163-88d8-381343337da1.9.23.0");var subQ1=sQuery(id+"F4.wireOp",EDGE,"f33b821f-3d74-4163-88d8-381343337da1.1.23.0");var subQ2=makeQuery(id+"F4.imprint","INTERSECT",VERTEX,{"derivedFrom":[subQ1,subQ0]});Q104=makeQuery(id+"F4.imprint","IMPRINT",FACE,{"disambiguationData":[TD([[makeQuery(id+"F4.imprint","IMPRINT",EDGE,{"disambiguationData":[TD([[subQ2,1.0]])],"derivedFrom":subQ1}),-1.0]])]});}
            var Q105;
            {var subQ0=sQuery(id+"F4.wireOp",EDGE,"E7.6.10.0");Q105=makeQuery(id+"F4.imprint","IMPRINT",FACE,{"disambiguationData":[TD([[makeQuery(id+"F4.imprint","IMPRINT",EDGE,{"derivedFrom":subQ0}),-1.0]])]});}
            var Q106;
            {var subQ0=sQuery(id+"F4.wireOp",EDGE,"E7.9.3.0");var subQ1=sQuery(id+"F4.wireOp",EDGE,"E7.1.3.0");var subQ2=makeQuery(id+"F4.imprint","INTERSECT",VERTEX,{"derivedFrom":[subQ1,subQ0]});Q106=makeQuery(id+"F4.imprint","IMPRINT",FACE,{"disambiguationData":[TD([[makeQuery(id+"F4.imprint","IMPRINT",EDGE,{"disambiguationData":[TD([[subQ2,1.0]])],"derivedFrom":subQ1}),-1.0]])]});}
            var Q107;
            {var subQ0=sQuery(id+"F4.wireOp",EDGE,"E7.9.11.0");var subQ1=sQuery(id+"F4.wireOp",EDGE,"E7.1.11.0");var subQ2=makeQuery(id+"F4.imprint","INTERSECT",VERTEX,{"derivedFrom":[subQ1,subQ0]});Q107=makeQuery(id+"F4.imprint","IMPRINT",FACE,{"disambiguationData":[TD([[makeQuery(id+"F4.imprint","IMPRINT",EDGE,{"disambiguationData":[TD([[subQ2,1.0]])],"derivedFrom":subQ1}),-1.0]])]});}
            var Q108;
            {var subQ0=sQuery(id+"F4.wireOp",EDGE,"E7.9.19.0");var subQ1=sQuery(id+"F4.wireOp",EDGE,"E7.1.19.0");var subQ2=makeQuery(id+"F4.imprint","INTERSECT",VERTEX,{"derivedFrom":[subQ1,subQ0]});Q108=makeQuery(id+"F4.imprint","IMPRINT",FACE,{"disambiguationData":[TD([[makeQuery(id+"F4.imprint","IMPRINT",EDGE,{"disambiguationData":[TD([[subQ2,1.0]])],"derivedFrom":subQ1}),-1.0]])]});}
            var Q109;
            {var subQ0=sQuery(id+"F4.wireOp",EDGE,"f33b821f-3d74-4163-88d8-381343337da1.9.27.0");var subQ1=sQuery(id+"F4.wireOp",EDGE,"f33b821f-3d74-4163-88d8-381343337da1.1.27.0");var subQ2=makeQuery(id+"F4.imprint","INTERSECT",VERTEX,{"derivedFrom":[subQ1,subQ0]});Q109=makeQuery(id+"F4.imprint","IMPRINT",FACE,{"disambiguationData":[TD([[makeQuery(id+"F4.imprint","IMPRINT",EDGE,{"disambiguationData":[TD([[subQ2,1.0]])],"derivedFrom":subQ1}),-1.0]])]});}
            var Q110;
            {var subQ4=sQuery(id+"F4.wireOp",EDGE,"E7.6.9.0");Q110=makeQuery(id+"F4.imprint","IMPRINT",FACE,{"disambiguationData":[TD([[makeQuery(id+"F4.imprint","IMPRINT",EDGE,{"derivedFrom":subQ4}),-1.0]])]});}
            var Q111;
            {var subQ0=sQuery(id+"F4.wireOp",EDGE,"E7.9.10.0");var subQ1=sQuery(id+"F4.wireOp",EDGE,"E7.3.10.0");var subQ2=makeQuery(id+"F4.imprint","INTERSECT",VERTEX,{"derivedFrom":[subQ1,subQ0]});Q111=makeQuery(id+"F4.imprint","IMPRINT",FACE,{"disambiguationData":[TD([[makeQuery(id+"F4.imprint","IMPRINT",EDGE,{"disambiguationData":[TD([[subQ2,-1.0]])],"derivedFrom":subQ1}),-1.0]])]});}
            var Q112;
            {var subQ0=sQuery(id+"F4.wireOp",EDGE,"E7.9.18.0");var subQ1=sQuery(id+"F4.wireOp",EDGE,"E7.3.18.0");var subQ2=makeQuery(id+"F4.imprint","INTERSECT",VERTEX,{"derivedFrom":[subQ1,subQ0]});Q112=makeQuery(id+"F4.imprint","IMPRINT",FACE,{"disambiguationData":[TD([[makeQuery(id+"F4.imprint","IMPRINT",EDGE,{"disambiguationData":[TD([[subQ2,-1.0]])],"derivedFrom":subQ1}),-1.0]])]});}
            var Q113;
            {var subQ0=sQuery(id+"F4.wireOp",EDGE,"f33b821f-3d74-4163-88d8-381343337da1.9.26.0");var subQ1=sQuery(id+"F4.wireOp",EDGE,"f33b821f-3d74-4163-88d8-381343337da1.3.26.0");var subQ2=makeQuery(id+"F4.imprint","INTERSECT",VERTEX,{"derivedFrom":[subQ1,subQ0]});Q113=makeQuery(id+"F4.imprint","IMPRINT",FACE,{"disambiguationData":[TD([[makeQuery(id+"F4.imprint","IMPRINT",EDGE,{"disambiguationData":[TD([[subQ2,-1.0]])],"derivedFrom":subQ1}),-1.0]])]});}
            var Q114;
            {var subQ0=sQuery(id+"F4.wireOp",EDGE,"E7.9.10.0");var subQ1=sQuery(id+"F4.wireOp",EDGE,"E7.1.10.0");var subQ2=makeQuery(id+"F4.imprint","INTERSECT",VERTEX,{"derivedFrom":[subQ1,subQ0]});Q114=makeQuery(id+"F4.imprint","IMPRINT",FACE,{"disambiguationData":[TD([[makeQuery(id+"F4.imprint","IMPRINT",EDGE,{"disambiguationData":[TD([[subQ2,1.0]])],"derivedFrom":subQ1}),-1.0]])]});}
            var Q115;
            {var subQ0=sQuery(id+"F4.wireOp",EDGE,"E7.9.18.0");var subQ1=sQuery(id+"F4.wireOp",EDGE,"E7.1.18.0");var subQ2=makeQuery(id+"F4.imprint","INTERSECT",VERTEX,{"derivedFrom":[subQ1,subQ0]});Q115=makeQuery(id+"F4.imprint","IMPRINT",FACE,{"disambiguationData":[TD([[makeQuery(id+"F4.imprint","IMPRINT",EDGE,{"disambiguationData":[TD([[subQ2,1.0]])],"derivedFrom":subQ1}),-1.0]])]});}
            var Q116;
            {var subQ0=sQuery(id+"F4.wireOp",EDGE,"f33b821f-3d74-4163-88d8-381343337da1.9.26.0");var subQ1=sQuery(id+"F4.wireOp",EDGE,"f33b821f-3d74-4163-88d8-381343337da1.1.26.0");var subQ2=makeQuery(id+"F4.imprint","INTERSECT",VERTEX,{"derivedFrom":[subQ1,subQ0]});Q116=makeQuery(id+"F4.imprint","IMPRINT",FACE,{"disambiguationData":[TD([[makeQuery(id+"F4.imprint","IMPRINT",EDGE,{"disambiguationData":[TD([[subQ2,1.0]])],"derivedFrom":subQ1}),-1.0]])]});}
            var Q117;
            {var subQ0=sQuery(id+"F4.wireOp",EDGE,"E7.9.9.0");var subQ1=sQuery(id+"F4.wireOp",EDGE,"E7.3.9.0");var subQ2=makeQuery(id+"F4.imprint","INTERSECT",VERTEX,{"derivedFrom":[subQ1,subQ0]});Q117=makeQuery(id+"F4.imprint","IMPRINT",FACE,{"disambiguationData":[TD([[makeQuery(id+"F4.imprint","IMPRINT",EDGE,{"disambiguationData":[TD([[subQ2,-1.0]])],"derivedFrom":subQ1}),-1.0]])]});}
            var Q118;
            {var subQ0=sQuery(id+"F4.wireOp",EDGE,"E7.9.9.0");var subQ1=sQuery(id+"F4.wireOp",EDGE,"E7.1.9.0");var subQ2=makeQuery(id+"F4.imprint","INTERSECT",VERTEX,{"derivedFrom":[subQ1,subQ0]});Q118=makeQuery(id+"F4.imprint","IMPRINT",FACE,{"disambiguationData":[TD([[makeQuery(id+"F4.imprint","IMPRINT",EDGE,{"disambiguationData":[TD([[subQ2,1.0]])],"derivedFrom":subQ1}),-1.0]])]});}
            var Q119;
            {var subQ0=sQuery(id+"F4.wireOp",EDGE,"f33b821f-3d74-4163-88d8-381343337da1.9.29.0");var subQ1=sQuery(id+"F4.wireOp",EDGE,"f33b821f-3d74-4163-88d8-381343337da1.1.29.0");var subQ2=makeQuery(id+"F4.imprint","INTERSECT",VERTEX,{"derivedFrom":[subQ1,subQ0]});Q119=makeQuery(id+"F4.imprint","IMPRINT",FACE,{"disambiguationData":[TD([[makeQuery(id+"F4.imprint","IMPRINT",EDGE,{"disambiguationData":[TD([[subQ2,1.0]])],"derivedFrom":subQ1}),-1.0]])]});}
            extrude(context, id + "F5", {"entities" : qUnion([Q0, Q1, Q2, Q3, Q4, Q5, Q6, Q7, Q8, Q9, Q10, Q11, Q12, Q13, Q14, Q15, Q16, Q17, Q18, Q19, Q20, Q21, Q22, Q23, Q24, Q25, Q26, Q27, Q28, Q29, Q30, Q31, Q32, Q33, Q34, Q35, Q36, Q37, Q38, Q39, Q40, Q41, Q42, Q43, Q44, Q45, Q46, Q47, Q48, Q49, Q50, Q51, Q52, Q53, Q54, Q55, Q56, Q57, Q58, Q59, Q60, Q61, Q62, Q63, Q64, Q65, Q66, Q67, Q68, Q69, Q70, Q71, Q72, Q73, Q74, Q75, Q76, Q77, Q78, Q79, Q80, Q81, Q82, Q83, Q84, Q85, Q86, Q87, Q88, Q89, Q90, Q91, Q92, Q93, Q94, Q95, Q96, Q97, Q98, Q99, Q100, Q101, Q102, Q103, Q104, Q105, Q106, Q107, Q108, Q109, Q110, Q111, Q112, Q113, Q114, Q115, Q116, Q117, Q118, Q119]), "operationType" : NewBodyOperationType.ADD, "oppositeDirection" : true, "depth" : 5 * mm});
        }
        {
            var Q0;
            Q0=makeQuery(id+"F5.opExtrude","SWEPT_EDGE",EDGE,{"disambiguationData":[OSD([sQuery(id+"F4.wireOp",EDGE,"E7.1.15.0"),sQuery(id+"F4.wireOp",EDGE,"E7.3.15.0")])]});
            var Q1;
            Q1=makeQuery(id+"F5.opExtrude","SWEPT_EDGE",EDGE,{"disambiguationData":[OSD([sQuery(id+"F4.wireOp",EDGE,"E7.1.14.0"),sQuery(id+"F4.wireOp",EDGE,"E7.3.14.0")])]});
            var Q2;
            Q2=makeQuery(id+"F5.opExtrude","SWEPT_EDGE",EDGE,{"disambiguationData":[OSD([sQuery(id+"F4.wireOp",EDGE,"E7.1.13.0"),sQuery(id+"F4.wireOp",EDGE,"E7.3.13.0")])]});
            var Q3;
            Q3=makeQuery(id+"F5.opExtrude","SWEPT_EDGE",EDGE,{"disambiguationData":[OSD([sQuery(id+"F4.wireOp",EDGE,"E7.1.12.0"),sQuery(id+"F4.wireOp",EDGE,"E7.3.12.0")])]});
            var Q4;
            Q4=makeQuery(id+"F5.opExtrude","SWEPT_EDGE",EDGE,{"disambiguationData":[OSD([sQuery(id+"F4.wireOp",EDGE,"E7.1.11.0"),sQuery(id+"F4.wireOp",EDGE,"E7.3.11.0")])]});
            var Q5;
            Q5=makeQuery(id+"F5.opExtrude","SWEPT_EDGE",EDGE,{"disambiguationData":[OSD([sQuery(id+"F4.wireOp",EDGE,"E7.1.10.0"),sQuery(id+"F4.wireOp",EDGE,"E7.3.10.0")])]});
            var Q6;
            Q6=makeQuery(id+"F5.opExtrude","SWEPT_EDGE",EDGE,{"disambiguationData":[OSD([sQuery(id+"F4.wireOp",EDGE,"E7.1.9.0"),sQuery(id+"F4.wireOp",EDGE,"E7.3.9.0")])]});
            var Q7;
            Q7=makeQuery(id+"F5.opExtrude","SWEPT_EDGE",EDGE,{"disambiguationData":[OSD([sQuery(id+"F4.wireOp",EDGE,"E7.1.16.0"),sQuery(id+"F4.wireOp",EDGE,"E7.3.16.0")])]});
            var Q8;
            Q8=makeQuery(id+"F5.opExtrude","SWEPT_EDGE",EDGE,{"disambiguationData":[OSD([sQuery(id+"F4.wireOp",EDGE,"E7.1.17.0"),sQuery(id+"F4.wireOp",EDGE,"E7.3.17.0")])]});
            var Q9;
            Q9=makeQuery(id+"F5.opExtrude","SWEPT_EDGE",EDGE,{"disambiguationData":[OSD([sQuery(id+"F4.wireOp",EDGE,"E7.1.18.0"),sQuery(id+"F4.wireOp",EDGE,"E7.3.18.0")])]});
            var Q10;
            Q10=makeQuery(id+"F5.opExtrude","SWEPT_EDGE",EDGE,{"disambiguationData":[OSD([sQuery(id+"F4.wireOp",EDGE,"E7.1.19.0"),sQuery(id+"F4.wireOp",EDGE,"E7.3.19.0")])]});
            var Q11;
            Q11=makeQuery(id+"F5.opExtrude","SWEPT_EDGE",EDGE,{"disambiguationData":[OSD([sQuery(id+"F4.wireOp",EDGE,"f33b821f-3d74-4163-88d8-381343337da1.1.21.0"),sQuery(id+"F4.wireOp",EDGE,"f33b821f-3d74-4163-88d8-381343337da1.3.21.0")])]});
            var Q12;
            Q12=makeQuery(id+"F5.opExtrude","SWEPT_EDGE",EDGE,{"disambiguationData":[OSD([sQuery(id+"F4.wireOp",EDGE,"f33b821f-3d74-4163-88d8-381343337da1.1.22.0"),sQuery(id+"F4.wireOp",EDGE,"f33b821f-3d74-4163-88d8-381343337da1.3.22.0")])]});
            var Q13;
            Q13=makeQuery(id+"F5.opExtrude","SWEPT_EDGE",EDGE,{"disambiguationData":[OSD([sQuery(id+"F4.wireOp",EDGE,"f33b821f-3d74-4163-88d8-381343337da1.1.23.0"),sQuery(id+"F4.wireOp",EDGE,"f33b821f-3d74-4163-88d8-381343337da1.3.23.0")])]});
            var Q14;
            Q14=makeQuery(id+"F5.opExtrude","SWEPT_EDGE",EDGE,{"disambiguationData":[OSD([sQuery(id+"F4.wireOp",EDGE,"f33b821f-3d74-4163-88d8-381343337da1.1.24.0"),sQuery(id+"F4.wireOp",EDGE,"f33b821f-3d74-4163-88d8-381343337da1.3.24.0")])]});
            var Q15;
            Q15=makeQuery(id+"F5.opExtrude","SWEPT_EDGE",EDGE,{"disambiguationData":[OSD([sQuery(id+"F4.wireOp",EDGE,"f33b821f-3d74-4163-88d8-381343337da1.1.25.0"),sQuery(id+"F4.wireOp",EDGE,"f33b821f-3d74-4163-88d8-381343337da1.3.25.0")])]});
            var Q16;
            Q16=makeQuery(id+"F5.opExtrude","SWEPT_EDGE",EDGE,{"disambiguationData":[OSD([sQuery(id+"F4.wireOp",EDGE,"f33b821f-3d74-4163-88d8-381343337da1.1.26.0"),sQuery(id+"F4.wireOp",EDGE,"f33b821f-3d74-4163-88d8-381343337da1.3.26.0")])]});
            var Q17;
            Q17=makeQuery(id+"F5.opExtrude","SWEPT_EDGE",EDGE,{"disambiguationData":[OSD([sQuery(id+"F4.wireOp",EDGE,"f33b821f-3d74-4163-88d8-381343337da1.1.27.0"),sQuery(id+"F4.wireOp",EDGE,"f33b821f-3d74-4163-88d8-381343337da1.3.27.0")])]});
            var Q18;
            Q18=makeQuery(id+"F5.opExtrude","SWEPT_EDGE",EDGE,{"disambiguationData":[OSD([sQuery(id+"F4.wireOp",EDGE,"f33b821f-3d74-4163-88d8-381343337da1.1.28.0"),sQuery(id+"F4.wireOp",EDGE,"f33b821f-3d74-4163-88d8-381343337da1.3.28.0")])]});
            var Q19;
            Q19=makeQuery(id+"F5.opExtrude","SWEPT_EDGE",EDGE,{"disambiguationData":[OSD([sQuery(id+"F4.wireOp",EDGE,"f33b821f-3d74-4163-88d8-381343337da1.1.29.0"),sQuery(id+"F4.wireOp",EDGE,"f33b821f-3d74-4163-88d8-381343337da1.3.29.0")])]});
            var Q20;
            Q20=makeQuery(id+"F5.opExtrude","SWEPT_EDGE",EDGE,{"disambiguationData":[OSD([sQuery(id+"F4.wireOp",EDGE,"E2"),sQuery(id+"F4.wireOp",EDGE,"E3")])]});
            var Q21;
            Q21=makeQuery(id+"F5.opExtrude","SWEPT_EDGE",EDGE,{"disambiguationData":[OSD([sQuery(id+"F4.wireOp",EDGE,"E6.1.0"),sQuery(id+"F4.wireOp",EDGE,"E6.1.1")])]});
            var Q22;
            Q22=makeQuery(id+"F5.opExtrude","SWEPT_EDGE",EDGE,{"disambiguationData":[OSD([sQuery(id+"F4.wireOp",EDGE,"E6.2.0"),sQuery(id+"F4.wireOp",EDGE,"E6.2.1")])]});
            var Q23;
            Q23=makeQuery(id+"F5.opExtrude","SWEPT_EDGE",EDGE,{"disambiguationData":[OSD([sQuery(id+"F4.wireOp",EDGE,"E7.1.3.0"),sQuery(id+"F4.wireOp",EDGE,"E7.3.3.0")])]});
            var Q24;
            Q24=makeQuery(id+"F5.opExtrude","SWEPT_EDGE",EDGE,{"disambiguationData":[OSD([sQuery(id+"F4.wireOp",EDGE,"E7.1.4.0"),sQuery(id+"F4.wireOp",EDGE,"E7.3.4.0")])]});
            var Q25;
            Q25=makeQuery(id+"F5.opExtrude","SWEPT_EDGE",EDGE,{"disambiguationData":[OSD([sQuery(id+"F4.wireOp",EDGE,"E7.1.5.0"),sQuery(id+"F4.wireOp",EDGE,"E7.3.5.0")])]});
            var Q26;
            Q26=makeQuery(id+"F5.opExtrude","SWEPT_EDGE",EDGE,{"disambiguationData":[OSD([sQuery(id+"F4.wireOp",EDGE,"E7.1.6.0"),sQuery(id+"F4.wireOp",EDGE,"E7.3.6.0")])]});
            var Q27;
            Q27=makeQuery(id+"F5.opExtrude","SWEPT_EDGE",EDGE,{"disambiguationData":[OSD([sQuery(id+"F4.wireOp",EDGE,"E7.1.7.0"),sQuery(id+"F4.wireOp",EDGE,"E7.3.7.0")])]});
            var Q28;
            Q28=makeQuery(id+"F5.opExtrude","SWEPT_EDGE",EDGE,{"disambiguationData":[OSD([sQuery(id+"F4.wireOp",EDGE,"E7.1.8.0"),sQuery(id+"F4.wireOp",EDGE,"E7.3.8.0")])]});
            var Q29;
            Q29=makeQuery(id+"F5.opExtrude","SWEPT_EDGE",EDGE,{"disambiguationData":[OSD([sQuery(id+"F4.wireOp",EDGE,"f33b821f-3d74-4163-88d8-381343337da1.1.20.0"),sQuery(id+"F4.wireOp",EDGE,"f33b821f-3d74-4163-88d8-381343337da1.3.20.0")])]});
            fillet(context, id + "F6", {"entities" : qUnion([Q0, Q1, Q2, Q3, Q4, Q5, Q6, Q7, Q8, Q9, Q10, Q11, Q12, Q13, Q14, Q15, Q16, Q17, Q18, Q19, Q20, Q21, Q22, Q23, Q24, Q25, Q26, Q27, Q28, Q29]), "radius" : 0.3 * mm, "tangentPropagation" : true, "allowEdgeOverflow" : false});
        }
        {
            var Q0;
            Q0=makeQuery(id+"F1.opExtrude","CAP_EDGE",EDGE,{"disambiguationData":[OSD([sQuery(id+"F0.wireOp",EDGE,"E0")])],"isStart":true});
            chamfer(context, id + "F7", {"entities" : qUnion([Q0]), "width" : 2.5 * mm, "tangentPropagation" : true});
        }
        {
            var Q0;
            {var subQ0=sQuery(id+"F0.wireOp",EDGE,"E0");Q0=makeQuery(id+"F7.opChamfer","BLEND_EDGE",EDGE,{"blendedFrom":[makeQuery(id+"F1.opExtrude","CAP_EDGE",EDGE,{"disambiguationData":[OSD([subQ0])],"isStart":true}),makeQuery(id+"F1.opExtrude","SWEPT_FACE",FACE,{"disambiguationData":[OSD([subQ0])]})],"blendedInto":[makeQuery(id+"F1.opExtrude","SWEPT_FACE",FACE,{"disambiguationData":[OSD([subQ0])]})]});}
            fillet(context, id + "F8", {"entities" : qUnion([Q0]), "radius" : 5 * mm, "tangentPropagation" : true, "allowEdgeOverflow" : false});
        }
    });
